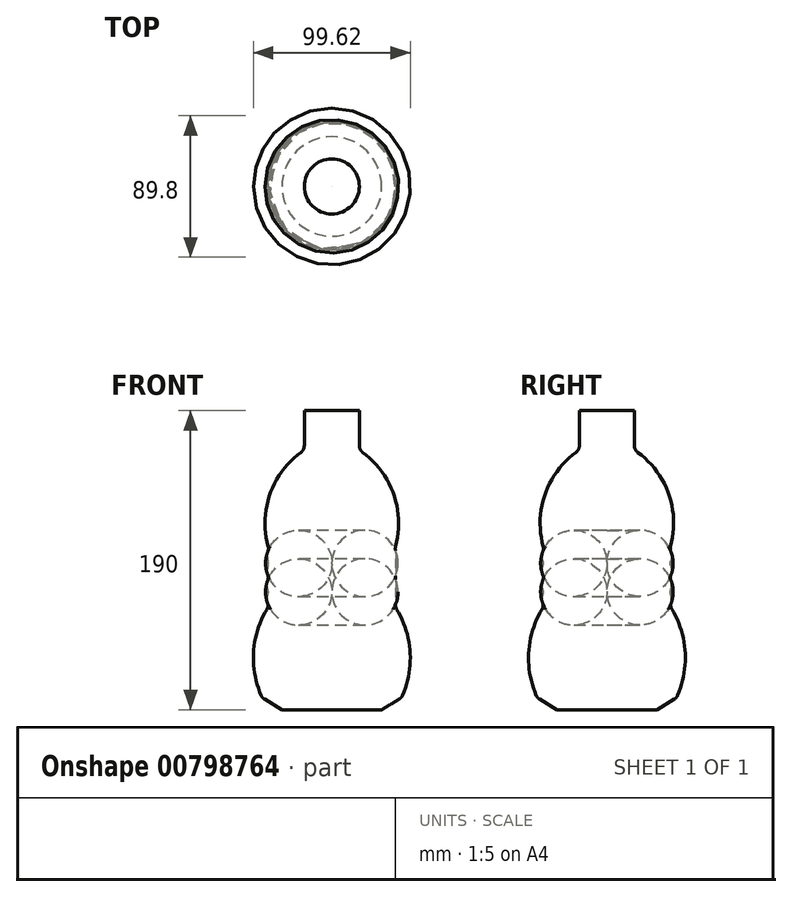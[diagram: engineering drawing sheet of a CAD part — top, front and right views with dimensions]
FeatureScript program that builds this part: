
annotation { "Feature Type Name" : "Feature", "Feature Type Description" : "" }
export const myFeature = defineFeature(function(context is Context, id is Id, definition is map)
    precondition{}
    {
        {
            var Q0;
            Q0=qCreatedBy(makeId("Front.planeOp"),FACE);
            var sketch = newSketch(context, id + "F0", { "sketchPlane" : qUnion([Q0])});
            skLineSegment(sketch, "E0", {"start": v(0, 97.8) * mm, "end": v(0, -92.2) * mm});
            skLineSegment(sketch, "E1", {"start": v(0, 97.8) * mm, "end": v(-17.5, 97.8) * mm});
            skLineSegment(sketch, "E2", {"start": v(0, -92.2) * mm, "end": v(-40, -92.2) * mm});
            skLineSegment(sketch, "E3", {"start": v(-17.5, 97.8) * mm, "end": v(-17.5, 72.8) * mm});
            skArc(sketch, "E4", {"start": v(-40, -26.4) * mm, "mid": v(-49.81, -59.3) * mm, "end": v(-40, -92.2) * mm});
            skArc(sketch, "E5", {"start": v(-17.5, 72.8) * mm, "mid": v(-39.14, 45.06) * mm, "end": v(-40, 9.88) * mm});
            skPoint(sketch, "E6", {"position": v(-40, -8.26) * mm});
            skPoint(sketch, "E7.first.point", {"position": v(0, 0) * mm});
            skArc(sketch, "E8", {"start": v(-40, -8.26) * mm, "mid": v(-40.07, -8.4) * mm, "end": v(-40.13, -8.55) * mm});
            skPoint(sketch, "E8.third.point", {"position": v(0, -17.5) * mm});
            skArc(sketch, "E9", {"start": v(-40, -8.26) * mm, "mid": v(-41.07, -12.88) * mm, "end": v(-40, -17.5) * mm});
            skPoint(sketch, "E9.first.point", {"position": v(-40, -17.5) * mm});
            skPoint(sketch, "E9.third.point", {"position": v(-21.03, -8.26) * mm});
            skArc(sketch, "E10", {"start": v(-40, -17.5) * mm, "mid": v(-40.99, -21.95) * mm, "end": v(-40, -26.4) * mm});
            skArc(sketch, "E11", {"start": v(-40, 0.8) * mm, "mid": v(-41.03, -3.73) * mm, "end": v(-40, -8.26) * mm});
            skPoint(sketch, "E11.third.point", {"position": v(-40, 0.8) * mm});
            skArc(sketch, "E12", {"start": v(-40, 9.88) * mm, "mid": v(-41.03, 5.34) * mm, "end": v(-40, 0.8) * mm});
            skArc(sketch, "E13.trimOffspring", {"start": v(0, 0) * mm, "mid": v(0.02, 0.8) * mm, "end": v(0, 1.62) * mm});
            skArc(sketch, "E14.trimOffspring", {"start": v(0, -17.5) * mm, "mid": v(0, -17.33) * mm, "end": v(0, -17.16) * mm});
            skSolve(sketch);
        }
        {
            var Q0;
            Q0 = qSketchRegion(id + "F0", true);
            var Q1;
            Q1=sQuery(id+"F0.wireOp",EDGE,"E0");
            revolve(context, id + "F1", {"surfaceOperationType" : NewSurfaceOperationType.NEW, "entities" : qUnion([Q0]), "axis" : qUnion([Q1]), "revolveType" : RevolveType.FULL});
        }
        {
            var Q0;
            Q0=makeQuery(id+"F1.opRevolve","SWEPT_EDGE",EDGE,{"disambiguationData":[OSD([sQuery(id+"F0.wireOp",EDGE,"E8"),sQuery(id+"F0.wireOp",EDGE,"E9"),sQuery(id+"F0.wireOp",EDGE,"E11")])]});
            var Q1;
            Q1=makeQuery(id+"F1.opRevolve","SWEPT_EDGE",EDGE,{"disambiguationData":[OSD([sQuery(id+"F0.wireOp",EDGE,"E9"),sQuery(id+"F0.wireOp",EDGE,"E10")])]});
            var Q2;
            Q2=makeQuery(id+"F1.opRevolve","SWEPT_EDGE",EDGE,{"disambiguationData":[OSD([sQuery(id+"F0.wireOp",EDGE,"E4"),sQuery(id+"F0.wireOp",EDGE,"E10")])]});
            var Q3;
            Q3=makeQuery(id+"F1.opRevolve","SWEPT_EDGE",EDGE,{"disambiguationData":[OSD([sQuery(id+"F0.wireOp",EDGE,"E11"),sQuery(id+"F0.wireOp",EDGE,"E12")])]});
            var Q4;
            Q4=makeQuery(id+"F1.opRevolve","SWEPT_EDGE",EDGE,{"disambiguationData":[OSD([sQuery(id+"F0.wireOp",EDGE,"E5"),sQuery(id+"F0.wireOp",EDGE,"E12")])]});
            fillet(context, id + "F2", {"entities" : qUnion([Q0, Q1, Q2, Q3, Q4]), "radius" : 5 * mm, "tangentPropagation" : true, "allowEdgeOverflow" : false});
        }
        {
            var Q0;
            Q0=makeQuery(id+"F1.opRevolve","SWEPT_EDGE",EDGE,{"disambiguationData":[OSD([sQuery(id+"F0.wireOp",EDGE,"E2"),sQuery(id+"F0.wireOp",EDGE,"E4")])]});
            chamfer(context, id + "F3", {"entities" : qUnion([Q0]), "chamferType" : ChamferType.OFFSET_ANGLE, "width" : 7 * mm, "oppositeDirection" : false, "angle" : 30 * degree, "tangentPropagation" : true});
        }
        {
            var Q0;
            {var subQ0=sQuery(id+"F0.wireOp",EDGE,"E4");Q0=makeQuery(id+"F3.opChamfer","BLEND_EDGE",EDGE,{"blendedFrom":[makeQuery(id+"F1.opRevolve","SWEPT_EDGE",EDGE,{"disambiguationData":[OSD([sQuery(id+"F0.wireOp",EDGE,"E2"),subQ0])]}),makeQuery(id+"F1.opRevolve","SWEPT_FACE",FACE,{"disambiguationData":[OSD([subQ0])]})],"blendedInto":[makeQuery(id+"F1.opRevolve","SWEPT_FACE",FACE,{"disambiguationData":[OSD([subQ0])]})]});}
            fillet(context, id + "F4", {"entities" : qUnion([Q0]), "radius" : 5 * mm, "tangentPropagation" : true, "allowEdgeOverflow" : false});
        }
        {
            var Q0;
            Q0=makeQuery(id+"F1.opRevolve","SWEPT_EDGE",EDGE,{"disambiguationData":[OSD([sQuery(id+"F0.wireOp",EDGE,"E3"),sQuery(id+"F0.wireOp",EDGE,"E5")])]});
            fillet(context, id + "F5", {"entities" : qUnion([Q0]), "radius" : 5 * mm, "tangentPropagation" : true, "allowEdgeOverflow" : false});
        }
    });
